# Revit family: Fireplaces_Gas_FireplaceX-Model-4415ST_10305648
name_source: partatom
category: Mechanical Equipment
units: mm (PartAtom-declared; Revit-internal decimal feet)

## family parameters
Always vertical = Yes
Classification Number = 23.75.00.00
Cut with Voids When Loaded = Yes
Maintain Annotation Orientation = No
Part Type = Normal
Room Calculation Point = No
Round Connector Dimension = Use Diameter
Shared = No
Work Plane-Based = Yes

## types (1)
- Fireplaces_Gas_FireplaceX-Model-4415ST_10305648
    Construction Details = https://www.arcat.com
    Cost = 0 $
    Default Elevation = 48"
    Electrical_Amperage = 7 A
    Electrical_Number of Poles = 1
    Electrical_Voltage = 120 V
    Exhaust Dia = 4"
    Fuel Type = LP
    Gas Connection Inlet Diameter = 3/4"
    Glass = Glass - DaVinci - Clear
    HVAC_BTU Input = 70000.0 Btu/h
    Keynote = 10 31 00
    Manufacturer = DaVinci Custom Fireplaces , Travis Industries Division
    Opening Height = 15 3/16"
    Product Page URL = https://www.arcat.com
    R = 2"
    Specification = https://www.arcat.com
    URL = https://www.davincifireplace.com
    Unit Depth = 16 9/32"
    Unit Height = 37 9/32"
    Unit Width = 51 3/16"

## geometry (parser evidence)
native form markers: Sweep x7
no freeform markers — native parametric forms only
